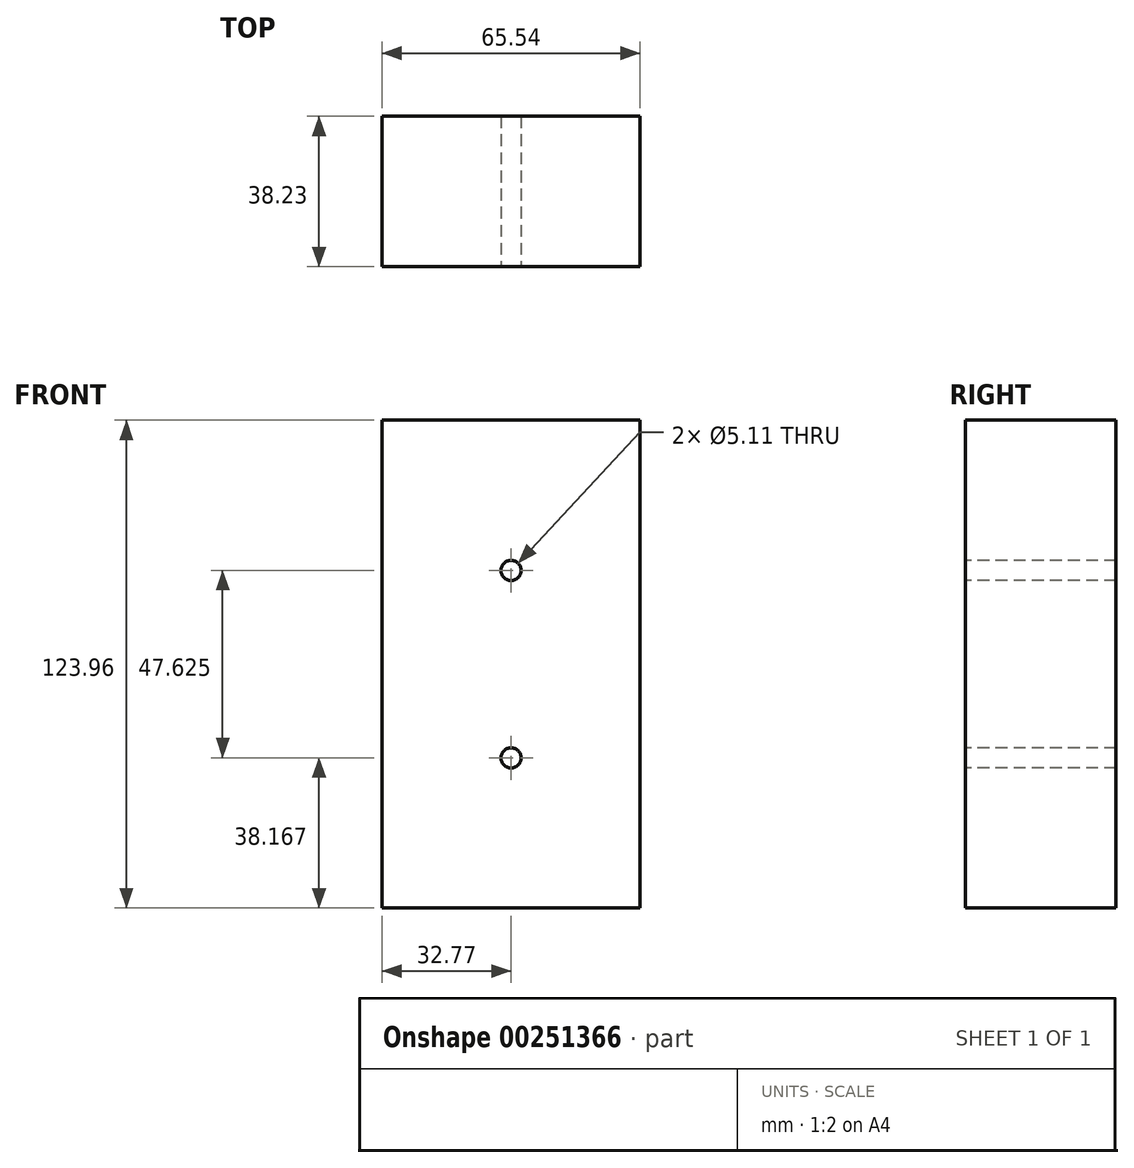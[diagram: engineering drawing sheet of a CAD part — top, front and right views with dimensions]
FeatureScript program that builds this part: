
annotation { "Feature Type Name" : "Feature", "Feature Type Description" : "" }
export const myFeature = defineFeature(function(context is Context, id is Id, definition is map)
    precondition{}
    {
        {
            var Q0;
            Q0=qCreatedBy(makeId("Front.planeOp"),FACE);
            var sketch = newSketch(context, id + "F0", { "sketchPlane" : qUnion([Q0])});
            skLineSegment(sketch, "E0.bottom", {"start": v(-32.77, 61.98) * mm, "end": v(32.77, 61.98) * mm});
            skLineSegment(sketch, "E0.top", {"start": v(-32.77, -61.98) * mm, "end": v(32.77, -61.98) * mm});
            skLineSegment(sketch, "E0.left", {"start": v(-32.77, 61.98) * mm, "end": v(-32.77, -61.98) * mm});
            skLineSegment(sketch, "E0.right", {"start": v(32.77, 61.98) * mm, "end": v(32.77, -61.98) * mm});
            skPoint(sketch, "E0.middle", {"position": v(0, 0) * mm});
            skSolve(sketch);
        }
        {
            var Q0;
            Q0 = qSketchRegion(id + "F0", true);
            extrude(context, id + "F1", {"entities" : qUnion([Q0]), "oppositeDirection" : true, "depth" : 38.23 * mm});
        }
        {
            var Q0;
            Q0=makeQuery(id+"F1.opExtrude","CAP_FACE",FACE,{"disambiguationData":[OSD([sQuery(id+"F0.wireOp",EDGE,"E0.bottom"),sQuery(id+"F0.wireOp",EDGE,"E0.top"),sQuery(id+"F0.wireOp",EDGE,"E0.left"),sQuery(id+"F0.wireOp",EDGE,"E0.right")])],"isStart":true});
            var sketch = newSketch(context, id + "F2", { "sketchPlane" : qUnion([Q0])});
            skLineSegment(sketch, "E1", {"start": v(0, 23.81) * mm, "end": v(0, -23.81) * mm, "construction": true});
            skSolve(sketch);
        }
        {
            var Q0;
            Q0=sQuery(id+"F2.wireOp",VERTEX,"E1.start");
            var Q1;
            Q1=sQuery(id+"F2.wireOp",VERTEX,"E1.end");
            var Q2;
            Q2=makeQuery(id+"F1.opExtrude","SWEPT_BODY",BODY,{"disambiguationData":[OSD([sQuery(id+"F0.wireOp",EDGE,"E0.bottom"),sQuery(id+"F0.wireOp",EDGE,"E0.top"),sQuery(id+"F0.wireOp",EDGE,"E0.left"),sQuery(id+"F0.wireOp",EDGE,"E0.right")])]});
            hole(context, id + "F3", {"style" : HoleStyle.SIMPLE, "endStyle" : HoleEndStyle.THROUGH, "standardTappedOrClearance" : lookupTablePath({ "standard" : "ANSI", "fit" : "Normal (ASME)", "size" : "#10", "type" : "Clearance" }), "standardBlindInLast" : lookupTablePath({ "fit" : "Free", "standard" : "ANSI", "size" : "#10", "type" : "Clearance" }), "holeDiameter" : 5.1 * mm, "tappedDepth" : 12.7 * mm, "tapClearance" : 3, "locations" : qUnion([Q0, Q1]), "scope" : qUnion([Q2])});
        }
    });
